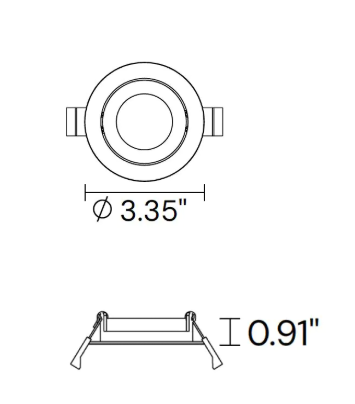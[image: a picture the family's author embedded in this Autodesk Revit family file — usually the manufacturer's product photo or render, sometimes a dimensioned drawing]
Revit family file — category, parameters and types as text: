
# Revit family: Alcon-14133-4 -Revit-Family
name_source: partatom
category: Lighting Fixtures
units: mm (PartAtom-declared; Revit-internal decimal feet)

## family parameters
Always vertical = Yes
Cut with Voids When Loaded = No
Host = Ceiling
Light Source = Yes
OmniClass Number = 23.80.70.11
OmniClass Title = Luminaries for Internal Lighting
Part Type = Normal
Room Calculation Point = No
Round Connector Dimension = Use Diameter
Shared = No

## types (1)
- Type 1
    Color Filter = 16777215
    Default Elevation = 0' - 0"
    Dimming Lamp Color Temperature Shift = <None>
    Emit Shape Visible in Rendering = No
    Emit from Circle Diameter = 0' - 4"
    Housing = Default
    Lens = Default
    Light Source Symbol Length = 10' - 0"
    LightSource = light
    Link To Product Page = https://www.alconlighting.com
    Manufacturer = Alcon Light
    Metal = <By Category>
    Product Identity = Alcon Lighting 14133-4
    Reflector = Default metal
    Spot Beam Angle = 30.00°
    Spot Field Angle = 90.00°
    Tilt Angle = 90.00°

## geometry (parser evidence)
native form markers: Sweep x2
no freeform markers — native parametric forms only
